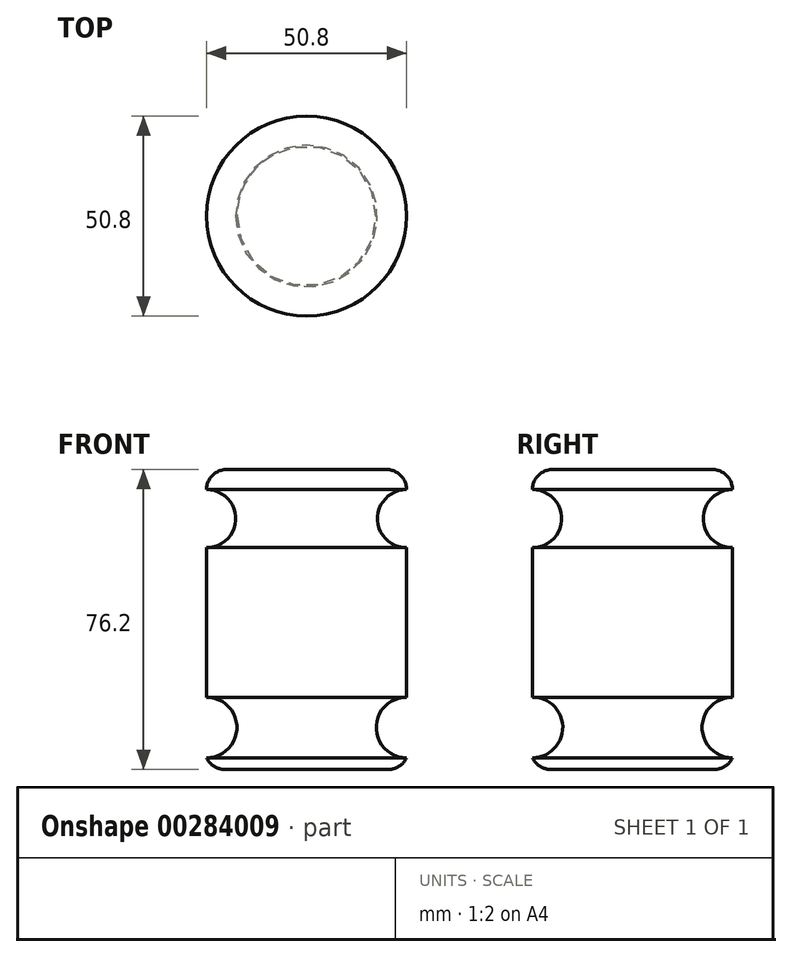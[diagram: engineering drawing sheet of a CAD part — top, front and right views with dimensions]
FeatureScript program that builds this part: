
annotation { "Feature Type Name" : "Feature", "Feature Type Description" : "" }
export const myFeature = defineFeature(function(context is Context, id is Id, definition is map)
    precondition{}
    {
        {
            var Q0;
            Q0=qCreatedBy(makeId("Front.planeOp"),FACE);
            var sketch = newSketch(context, id + "F0", { "sketchPlane" : qUnion([Q0])});
            skLineSegment(sketch, "E0.bottom", {"start": v(-3.5, 2.86) * mm, "end": v(-28.9, 2.86) * mm});
            skLineSegment(sketch, "E0.top", {"start": v(-3.5, 79.06) * mm, "end": v(-28.9, 79.06) * mm});
            skLineSegment(sketch, "E0.left", {"start": v(-3.5, 2.86) * mm, "end": v(-3.5, 5.82) * mm});
            skLineSegment(sketch, "E0.right", {"start": v(-28.9, 2.86) * mm, "end": v(-28.9, 79.06) * mm});
            skArc(sketch, "E1", {"start": v(-3.5, 73.98) * mm, "mid": v(-10.9, 66.6) * mm, "end": v(-3.5, 59.2) * mm});
            skArc(sketch, "E2", {"start": v(-3.5, 21.22) * mm, "mid": v(-11.2, 13.52) * mm, "end": v(-3.5, 5.82) * mm});
            skLineSegment(sketch, "E3.trimOffspring", {"start": v(-3.5, 73.98) * mm, "end": v(-3.5, 79.06) * mm});
            skLineSegment(sketch, "E4.trimOffspring", {"start": v(-3.5, 21.22) * mm, "end": v(-3.5, 59.2) * mm});
            skSolve(sketch);
        }
        {
            var Q0;
            Q0 = qSketchRegion(id + "F0", true);
            var Q1;
            Q1=sQuery(id+"F0.wireOp",EDGE,"E0.right");
            revolve(context, id + "F1", {"entities" : qUnion([Q0]), "axis" : qUnion([Q1]), "revolveType" : RevolveType.FULL});
        }
        {
            var Q0;
            Q0=makeQuery(id+"F1.opRevolve","SWEPT_EDGE",EDGE,{"disambiguationData":[OSD([sQuery(id+"F0.wireOp",EDGE,"E0.top"),sQuery(id+"F0.wireOp",EDGE,"E3.trimOffspring")])]});
            var Q1;
            Q1=makeQuery(id+"F1.opRevolve","SWEPT_EDGE",EDGE,{"disambiguationData":[OSD([sQuery(id+"F0.wireOp",EDGE,"E0.bottom"),sQuery(id+"F0.wireOp",EDGE,"E0.left")])]});
            fillet(context, id + "F2", {"entities" : qUnion([Q0, Q1]), "radius" : 5.08 * mm, "tangentPropagation" : true, "allowEdgeOverflow" : false});
        }
    });
